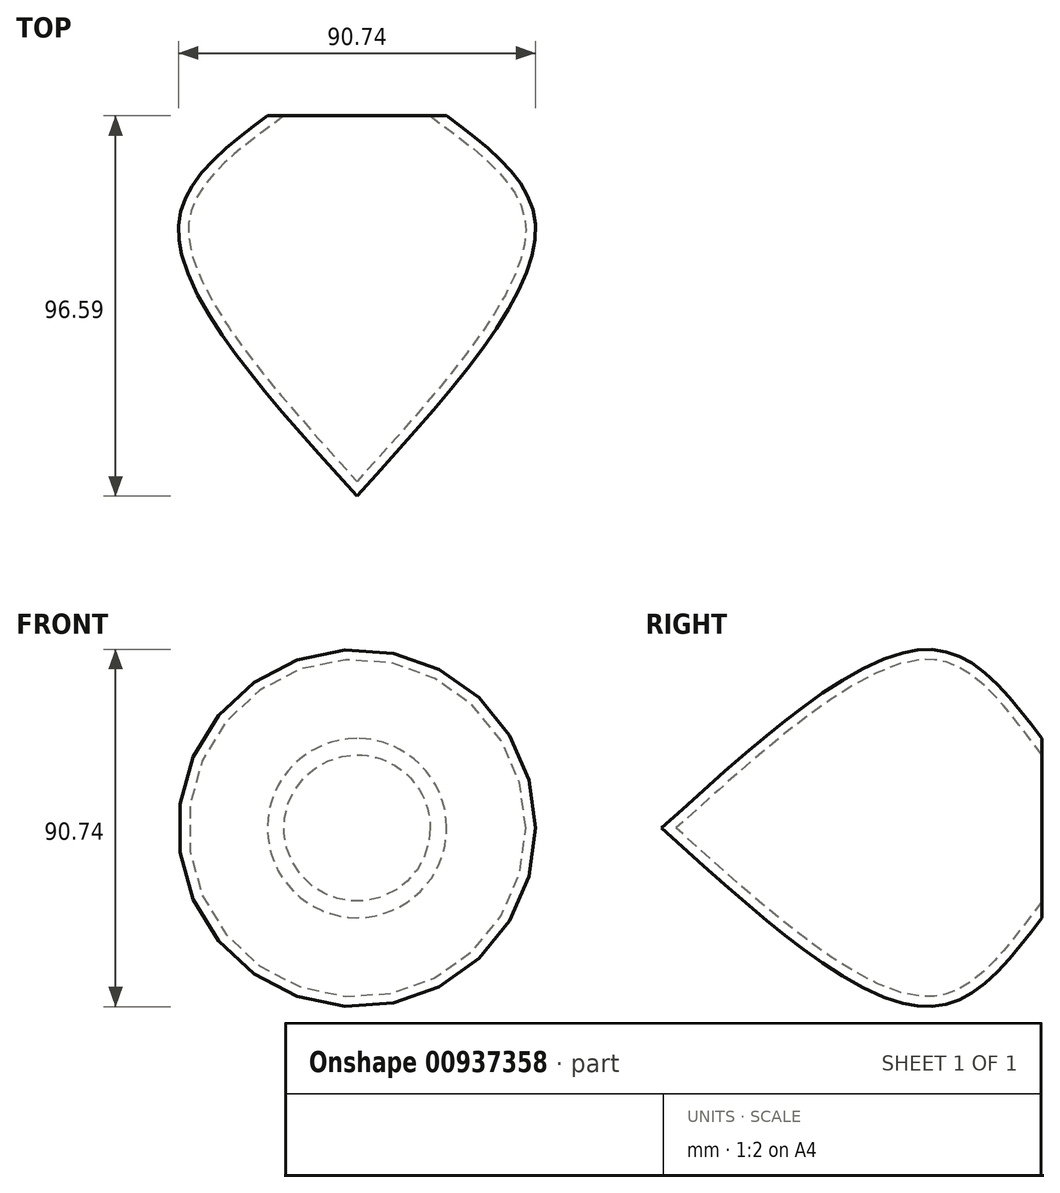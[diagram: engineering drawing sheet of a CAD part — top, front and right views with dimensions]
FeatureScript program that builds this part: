
annotation { "Feature Type Name" : "Feature", "Feature Type Description" : "" }
export const myFeature = defineFeature(function(context is Context, id is Id, definition is map)
    precondition{}
    {
        {
            var Q0;
            Q0=qCreatedBy(makeId("Top.planeOp"),FACE);
            var sketch = newSketch(context, id + "F0", { "sketchPlane" : qUnion([Q0])});
            skLineSegment(sketch, "E0", {"start": v(0, 0) * mm, "end": v(0, -96.6) * mm});
            skLineSegment(sketch, "E1", {"start": v(0, 0) * mm, "end": v(22.76, 0) * mm});
            skFitSpline(sketch, "E2", {"points": [v(22.76, 0) * mm, v(45.35, -28.14) * mm, v(0, -96.6) * mm], "startDerivative": vector(83, -61.97) * mm, "endDerivative": vector(-115.13, -126.83) * mm});
            skSolve(sketch);
        }
        {
            var Q0;
            Q0=makeQuery(id+"F0.imprint","IMPRINT",FACE,{"disambiguationData":[TD([[makeQuery(id+"F0.imprint","IMPRINT",EDGE,{"derivedFrom":sQuery(id+"F0.wireOp",EDGE,"E0")}),1.0]])]});
            var Q1;
            Q1=sQuery(id+"F0.wireOp",EDGE,"E0");
            revolve(context, id + "F1", {"surfaceOperationType" : NewSurfaceOperationType.NEW, "entities" : qUnion([Q0]), "axis" : qUnion([Q1]), "revolveType" : RevolveType.FULL});
        }
        {
            var Q0;
            Q0=makeQuery(id+"F1.opRevolve","SWEPT_FACE",FACE,{"disambiguationData":[OSD([sQuery(id+"F0.wireOp",EDGE,"E1")])]});
            shell(context, id + "F2", {"entities" : qUnion([Q0]), "thickness" : 2.5 * mm});
        }
    });
